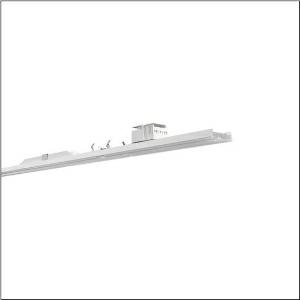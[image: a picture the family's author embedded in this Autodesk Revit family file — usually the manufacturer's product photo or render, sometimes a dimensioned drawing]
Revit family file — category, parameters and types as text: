
# Revit family: licross_r__11_recessed_mo_51tl14dn485fd_8955
name_source: partatom
category: Lighting Fixtures
units: mm (PartAtom-declared; Revit-internal decimal feet)

## family parameters
Cut with Voids When Loaded = No
Host = Face
Light Source = No
Part Type = Normal
Room Calculation Point = No
Round Connector Dimension = Use Diameter
Shared = No

## types (1)
- --- (1 x LED, 1360 lm, 9.8 W, 4000K)
    Apparent Load = 10 VA
    CIE Flux Codes = 56 84 97 100 100
    Color Rendering = 80
    Color Temperature = 4000K
    Default Elevation = 1800 mm
    Description = Licross® 11 Recessed MOluminaire insert, length: 1.500mm, width: 66mm, height: 67mm, LED rated luminous flux: 8.550lm, light colour: 840, control gear: DALI 2, control gear: ECG DALI, with plug, 6-pole, with phase selection, mains connection: 220..240V, AC/DC, 0/50..60Hz, without changeover relay, for emergency light function, for central battery installations according to DIN EN 60598-2-22, halogen-free wiring, primary optical cover: cover, of PMMA, light emission: direct distribution, primary light characteristic: asymmetric, protection rating (complete): IP40, insulation class (complete): insulation class I (protective earthing), certification: CE, ENEC, VDE, protection symbol: D if used in an environment without relevant dust loads with corresponding accessories, permissible ambient temperature for indoor applications: -25..+35°C, standard: EN 60598-2-22, reducing of maximum allowable ambient temperature of 5°C with ceiling mounting, corresponds to IFS (International Featured Standards) requirements for safety and quality in the food industry, packaging unit: 1 piece
    Height = 58 mm
    Lamp = 1 x LED
    Lamp Light Flux = 1360 lm
    Lamp Power = 9.8 W
    Lamp count = 1
    Length = 1500 mm
    Luminous efficacy = 139 lm/W
    Manufacturer = Siteco
    ModVariant = No
    Model = 51TL14DN485FD
    Mounting Place = Ceiling
    Mounting Type = Pendant
    Number of Poles = 1
    OnlyDefault = Yes
    Power Factor = 1
    Product Name = Licross® 11 Recessed MO
    Product group = luminaire insert
    ProductGroupID = 902
    Protection Class = Protection class I
    Protection Degree = IP 40
    RLX_Detail_Level = 1
    RlxData = <blob elided: 23157 chars, md5=bf4363ab>
    Socket = socket
    Standby Power = 0 W
    System Light Flux = 1360 lm
    System Power = 10 W
    Type Comments = : DC mode (central or group accumulator) initial emergency light level
    Type Image = l_1266722.jpg
    URL = http://relux.com
    VarID = @adj_134349
    Voltage = 0 V
    Weight = 0.00 kg
    Width = 66 mm

## geometry (parser evidence)
native form markers: Blend x4, Sweep x12
no freeform markers — native parametric forms only
